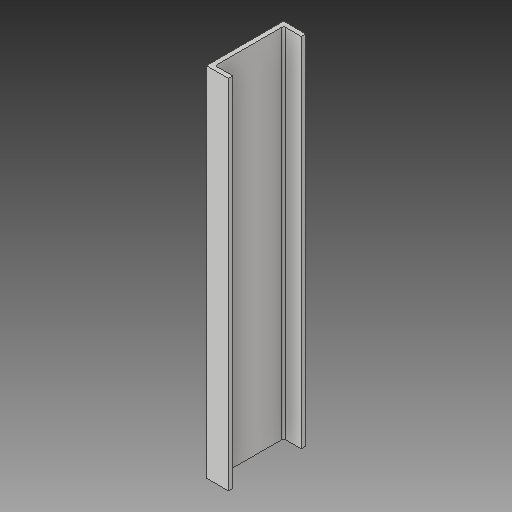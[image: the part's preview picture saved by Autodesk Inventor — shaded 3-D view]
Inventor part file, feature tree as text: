
AUTODESK INVENTOR PART (.ipt)
format: ipt  version: 2019 (Build 230136000, 136)  size: 102,912 bytes
history: native  units: in
note: dims shown in document units (in); Inventor stores cm internally (conversion verified against a paired STEP export)
features: other x3, sketch x3
ambient origin geometry x8: Origin, YZ Plane, XZ Plane, XY Plane, X Axis, Y Axis, Z Axis, Center Point
bodies: Solid1 (feature_tree)
feature tree (6):
  other  "Base1.ipt"
  other  "Solid1::Base1.ipt"
  other  "TaggingFeature1"
  sketch  "Sketch1"  dims[d0=0.3937in]
  sketch  "Sketch2"
  sketch  "Sketch3"
